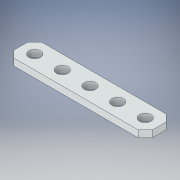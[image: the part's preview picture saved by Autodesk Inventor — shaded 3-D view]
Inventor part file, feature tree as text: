
AUTODESK INVENTOR PART (.ipt)
format: ipt  version: 2018 (Build 220112000, 112)  size: 121,344 bytes
history: native  units: in
note: dims shown in document units (in); Inventor stores cm internally (conversion verified against a paired STEP export)
features: chamfer x1
ambient origin geometry x8: Origin, YZ Plane, XZ Plane, XY Plane, X Axis, Y Axis, Z Axis, Center Point
bodies: Solid1 (feature_tree)
feature tree (1):
  chamfer  "Chamfer1"  [1 undecoded]
note: 1 required parameter value undecoded (feature->parameter linkage not recoverable at this tier; creation-order binding heuristic only, values carry confidence <= 0.55)
